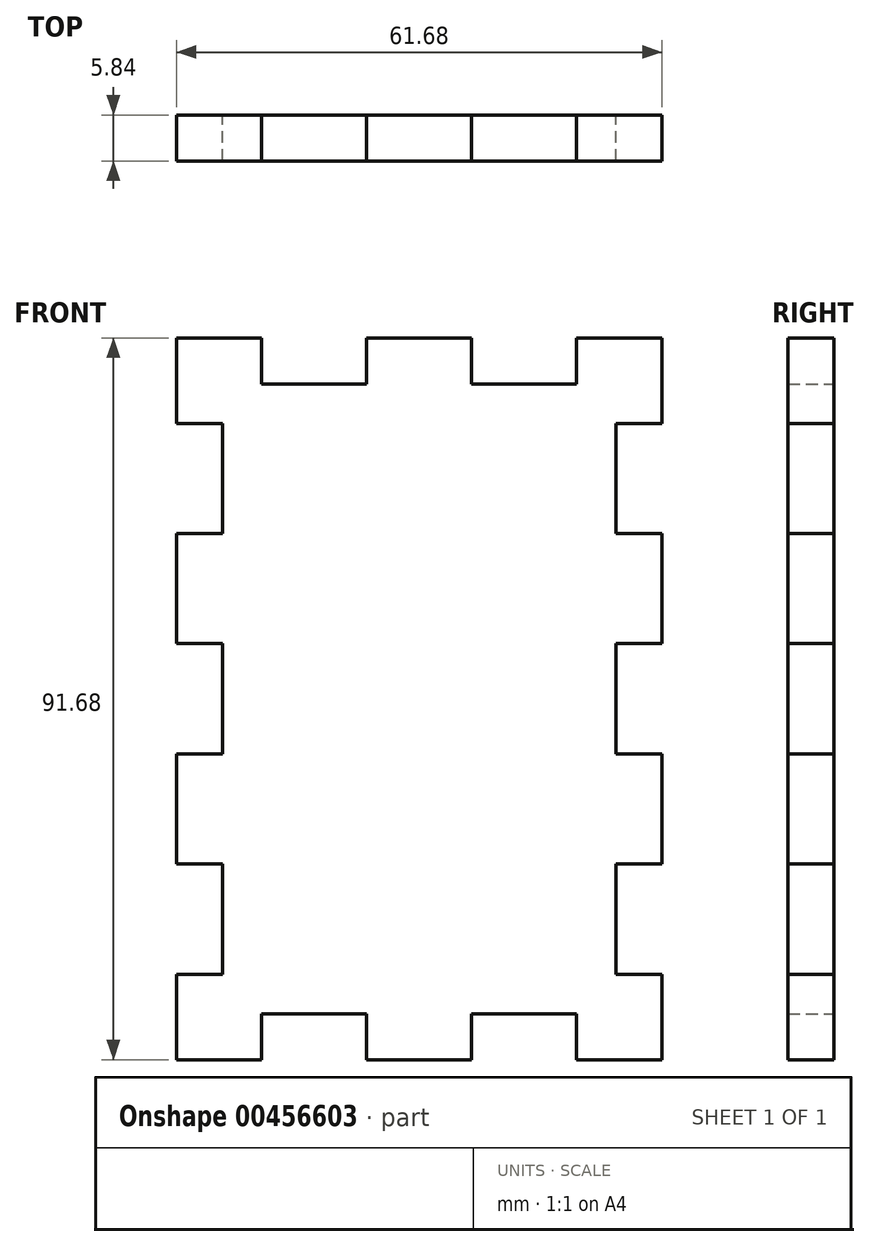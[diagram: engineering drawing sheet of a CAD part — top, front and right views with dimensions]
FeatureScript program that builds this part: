
annotation { "Feature Type Name" : "Feature", "Feature Type Description" : "" }
export const myFeature = defineFeature(function(context is Context, id is Id, definition is map)
    precondition{}
    {
        {
            var Q0;
            Q0=qCreatedBy(makeId("Front.planeOp"),FACE);
            var sketch = newSketch(context, id + "F0", { "sketchPlane" : qUnion([Q0])});
            skLineSegment(sketch, "E0.bottom", {"start": v(-20, -40) * mm, "end": v(-6.67, -40) * mm});
            skLineSegment(sketch, "E0.top", {"start": v(-20, 40) * mm, "end": v(-6.67, 40) * mm});
            skLineSegment(sketch, "E0.left", {"start": v(-25, -35) * mm, "end": v(-25, -21) * mm});
            skLineSegment(sketch, "E0.right", {"start": v(25, -35) * mm, "end": v(25, -21) * mm});
            skLineSegment(sketch, "E1.bottom", {"start": v(-30.84, 45.84) * mm, "end": v(-20, 45.84) * mm});
            skLineSegment(sketch, "E1.top", {"start": v(-30.84, -45.84) * mm, "end": v(-20, -45.84) * mm});
            skLineSegment(sketch, "E1.left", {"start": v(-30.84, 45.84) * mm, "end": v(-30.84, 35) * mm});
            skLineSegment(sketch, "E1.right", {"start": v(30.84, 45.84) * mm, "end": v(30.84, 35) * mm});
            skLineSegment(sketch, "E2.top", {"start": v(-30.84, 35) * mm, "end": v(-25, 35) * mm});
            skLineSegment(sketch, "E2.right", {"start": v(-20, 45.84) * mm, "end": v(-20, 40) * mm});
            skLineSegment(sketch, "E3.bottom", {"start": v(30.84, 45.84) * mm, "end": v(20, 45.84) * mm});
            skLineSegment(sketch, "E3.top", {"start": v(30.84, 35) * mm, "end": v(25, 35) * mm});
            skLineSegment(sketch, "E3.right", {"start": v(20, 45.84) * mm, "end": v(20, 40) * mm});
            skLineSegment(sketch, "E4.top", {"start": v(-6.67, 45.84) * mm, "end": v(6.67, 45.84) * mm});
            skLineSegment(sketch, "E4.left", {"start": v(-6.67, 40) * mm, "end": v(-6.67, 45.84) * mm});
            skLineSegment(sketch, "E4.right", {"start": v(6.67, 40) * mm, "end": v(6.67, 45.84) * mm});
            skLineSegment(sketch, "E5.top", {"start": v(-30.84, -35) * mm, "end": v(-25, -35) * mm});
            skLineSegment(sketch, "E5.left", {"start": v(-30.84, -45.84) * mm, "end": v(-30.84, -35) * mm});
            skLineSegment(sketch, "E5.right", {"start": v(-20, -45.84) * mm, "end": v(-20, -40) * mm});
            skLineSegment(sketch, "E6.bottom", {"start": v(30.84, -45.84) * mm, "end": v(20, -45.84) * mm});
            skLineSegment(sketch, "E6.top", {"start": v(30.84, -35) * mm, "end": v(25, -35) * mm});
            skLineSegment(sketch, "E6.left", {"start": v(30.84, -45.84) * mm, "end": v(30.84, -35) * mm});
            skLineSegment(sketch, "E6.right", {"start": v(20, -45.84) * mm, "end": v(20, -40) * mm});
            skLineSegment(sketch, "E7.bottom", {"start": v(-6.67, -45.84) * mm, "end": v(6.67, -45.84) * mm});
            skLineSegment(sketch, "E7.left", {"start": v(-6.67, -45.84) * mm, "end": v(-6.67, -40) * mm});
            skLineSegment(sketch, "E7.right", {"start": v(6.67, -45.84) * mm, "end": v(6.67, -40) * mm});
            skLineSegment(sketch, "E8.bottom", {"start": v(-30.84, 21) * mm, "end": v(-25, 21) * mm});
            skLineSegment(sketch, "E8.top", {"start": v(-30.84, 7) * mm, "end": v(-25, 7) * mm});
            skLineSegment(sketch, "E8.left", {"start": v(-30.84, 21) * mm, "end": v(-30.84, 7) * mm});
            skLineSegment(sketch, "E9.bottom", {"start": v(-30.84, -7) * mm, "end": v(-25, -7) * mm});
            skLineSegment(sketch, "E9.top", {"start": v(-30.84, -21) * mm, "end": v(-25, -21) * mm});
            skLineSegment(sketch, "E9.left", {"start": v(-30.84, -7) * mm, "end": v(-30.84, -21) * mm});
            skLineSegment(sketch, "E10.bottom", {"start": v(25, 21) * mm, "end": v(30.84, 21) * mm});
            skLineSegment(sketch, "E10.top", {"start": v(25, 7) * mm, "end": v(30.84, 7) * mm});
            skLineSegment(sketch, "E10.right", {"start": v(30.84, 21) * mm, "end": v(30.84, 7) * mm});
            skLineSegment(sketch, "E11.bottom", {"start": v(25, -7) * mm, "end": v(30.84, -7) * mm});
            skLineSegment(sketch, "E11.top", {"start": v(25, -21) * mm, "end": v(30.84, -21) * mm});
            skLineSegment(sketch, "E11.right", {"start": v(30.84, -7) * mm, "end": v(30.84, -21) * mm});
            skLineSegment(sketch, "E12.trimOffspring", {"start": v(-30.84, -35) * mm, "end": v(-30.84, -45.84) * mm});
            skLineSegment(sketch, "E13.trimOffspring", {"start": v(30.84, -35) * mm, "end": v(30.84, -45.84) * mm});
            skLineSegment(sketch, "E14.trimOffspring", {"start": v(20, 45.84) * mm, "end": v(30.84, 45.84) * mm});
            skLineSegment(sketch, "E15.trimOffspring", {"start": v(6.67, 40) * mm, "end": v(20, 40) * mm});
            skLineSegment(sketch, "E16.trimOffspring", {"start": v(25, 21) * mm, "end": v(25, 35) * mm});
            skLineSegment(sketch, "E17.trimOffspring", {"start": v(25, -7) * mm, "end": v(25, 7) * mm});
            skLineSegment(sketch, "E18.trimOffspring", {"start": v(-25, -7) * mm, "end": v(-25, 7) * mm});
            skLineSegment(sketch, "E19.trimOffspring", {"start": v(-25, 21) * mm, "end": v(-25, 35) * mm});
            skLineSegment(sketch, "E20.trimOffspring", {"start": v(20, -45.84) * mm, "end": v(30.84, -45.84) * mm});
            skLineSegment(sketch, "E21.trimOffspring", {"start": v(6.67, -40) * mm, "end": v(20, -40) * mm});
            skSolve(sketch);
        }
        {
            var Q0;
            Q0 = qSketchRegion(id + "F0", true);
            extrude(context, id + "F1", {"entities" : qUnion([Q0]), "depth" : 5.84 * mm});
        }
    });
